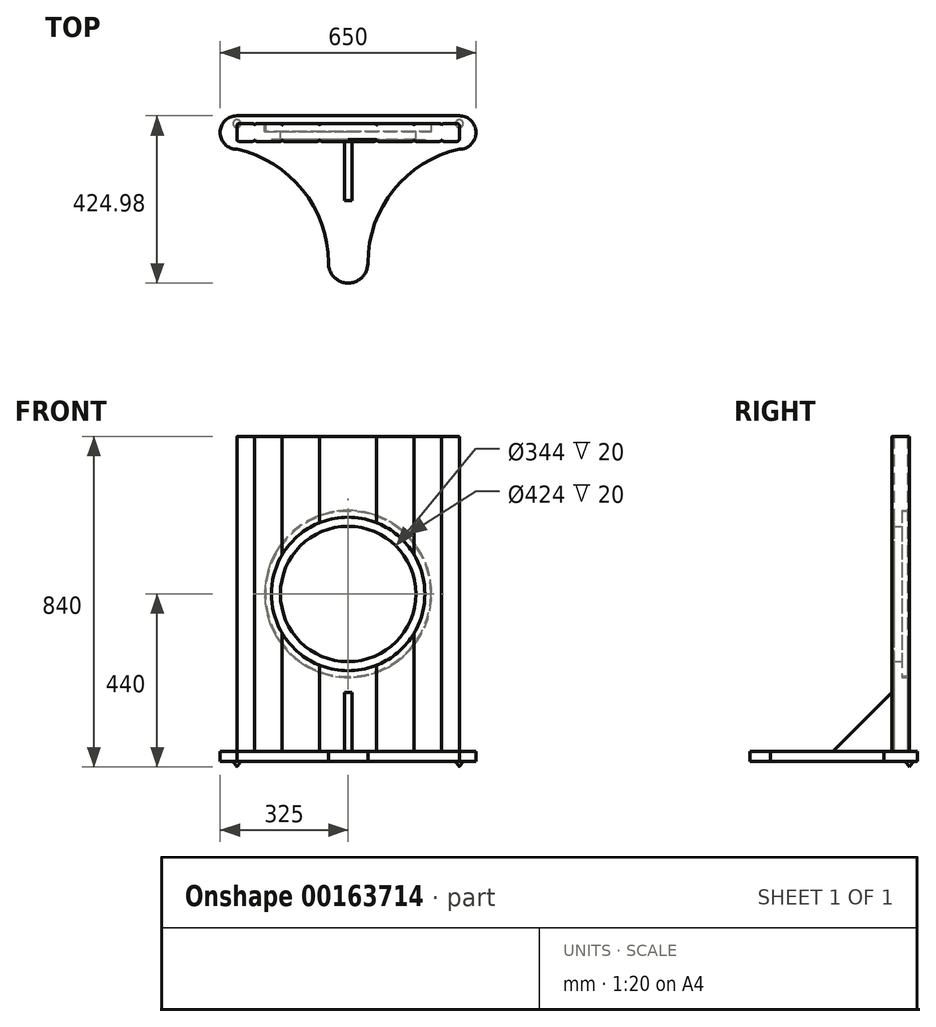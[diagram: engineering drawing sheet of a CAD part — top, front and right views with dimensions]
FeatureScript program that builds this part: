
annotation { "Feature Type Name" : "Feature", "Feature Type Description" : "" }
export const myFeature = defineFeature(function(context is Context, id is Id, definition is map)
    precondition{}
    {
        {
            var Q0;
            Q0=qCreatedBy(makeId("Top.planeOp"),FACE);
            var sketch = newSketch(context, id + "F0", { "sketchPlane" : qUnion([Q0])});
            skLineSegment(sketch, "E0.bottom", {"start": v(67.5, -22.5) * mm, "end": v(-67.5, -22.5) * mm});
            skLineSegment(sketch, "E0.top", {"start": v(67.5, 22.5) * mm, "end": v(-67.5, 22.5) * mm});
            skLineSegment(sketch, "E0.left", {"start": v(72.5, -17.5) * mm, "end": v(72.5, 17.5) * mm});
            skLineSegment(sketch, "E0.right", {"start": v(-72.5, -17.5) * mm, "end": v(-72.5, 17.5) * mm});
            skPoint(sketch, "E0.middle", {"position": v(0, 0) * mm});
            skPoint(sketch, "E1.visualSharp", {"position": v(-72.5, 22.5) * mm});
            skArc(sketch, "E1.filletArc", {"start": v(-67.5, 22.5) * mm, "mid": v(-71.04, 21.04) * mm, "end": v(-72.5, 17.5) * mm});
            skPoint(sketch, "E2.visualSharp", {"position": v(72.5, 22.5) * mm});
            skArc(sketch, "E2.filletArc", {"start": v(72.5, 17.5) * mm, "mid": v(71.04, 21.04) * mm, "end": v(67.5, 22.5) * mm});
            skPoint(sketch, "E3.visualSharp", {"position": v(72.5, -22.5) * mm});
            skArc(sketch, "E3.filletArc", {"start": v(67.5, -22.5) * mm, "mid": v(71.04, -21.04) * mm, "end": v(72.5, -17.5) * mm});
            skPoint(sketch, "E4.visualSharp", {"position": v(-72.5, -22.5) * mm});
            skArc(sketch, "E4.filletArc", {"start": v(-72.5, -17.5) * mm, "mid": v(-71.04, -21.04) * mm, "end": v(-67.5, -22.5) * mm});
            skSolve(sketch);
        }
        {
            var Q0;
            Q0 = qSketchRegion(id + "F0", true);
            extrude(context, id + "F1", {"entities" : qUnion([Q0]), "depth" : 800 * mm});
        }
        {
            var Q0;
            Q0=makeQuery(id+"F1.opExtrude","SWEPT_FACE",FACE,{"disambiguationData":[OSD([sQuery(id+"F0.wireOp",EDGE,"E0.right")])]});
            var sketch = newSketch(context, id + "F2", { "sketchPlane" : qUnion([Q0])});
            skLineSegment(sketch, "E5", {"start": v(-17.5, 0) * mm, "end": v(382.5, 0) * mm});
            skLineSegment(sketch, "E6", {"start": v(382.5, 0) * mm, "end": v(382.5, 50) * mm});
            skLineSegment(sketch, "E7", {"start": v(-17.5, 0) * mm, "end": v(-17.5, 500) * mm});
            skLineSegment(sketch, "E8", {"start": v(-17.5, 500) * mm, "end": v(17.5, 500) * mm});
            skArc(sketch, "E9", {"start": v(17.5, 500) * mm, "mid": v(117.94, 208.44) * mm, "end": v(382.5, 50) * mm});
            skSolve(sketch);
        }
        {
            var Q0;
            Q0 = qSketchRegion(id + "F2", true);
            extrude(context, id + "F3", {"entities" : qUnion([Q0]), "depth" : 10 * mm});
        }
        {
            var Q0;
            Q0=qCreatedBy(makeId("Top.planeOp"),FACE);
            var sketch = newSketch(context, id + "F4", { "sketchPlane" : qUnion([Q0])});
            skLineSegment(sketch, "E10.bottom", {"start": v(42.5, -22.5) * mm, "end": v(-42.5, -22.5) * mm});
            skLineSegment(sketch, "E10.top", {"start": v(42.5, 22.5) * mm, "end": v(-42.5, 22.5) * mm});
            skLineSegment(sketch, "E10.left", {"start": v(47.5, -17.5) * mm, "end": v(47.5, 17.5) * mm});
            skLineSegment(sketch, "E10.right", {"start": v(-47.5, -17.5) * mm, "end": v(-47.5, 17.5) * mm});
            skPoint(sketch, "E10.middle", {"position": v(0, 0) * mm});
            skPoint(sketch, "E11.visualSharp", {"position": v(-47.5, 22.5) * mm});
            skArc(sketch, "E11.filletArc", {"start": v(-42.5, 22.5) * mm, "mid": v(-46.04, 21.04) * mm, "end": v(-47.5, 17.5) * mm});
            skPoint(sketch, "E12.visualSharp", {"position": v(47.5, 22.5) * mm});
            skArc(sketch, "E12.filletArc", {"start": v(47.5, 17.5) * mm, "mid": v(46.04, 21.04) * mm, "end": v(42.5, 22.5) * mm});
            skPoint(sketch, "E13.visualSharp", {"position": v(47.5, -22.5) * mm});
            skArc(sketch, "E13.filletArc", {"start": v(42.5, -22.5) * mm, "mid": v(46.04, -21.04) * mm, "end": v(47.5, -17.5) * mm});
            skPoint(sketch, "E14.visualSharp", {"position": v(-47.5, -22.5) * mm});
            skArc(sketch, "E14.filletArc", {"start": v(-47.5, -17.5) * mm, "mid": v(-46.04, -21.04) * mm, "end": v(-42.5, -22.5) * mm});
            skSolve(sketch);
        }
        {
            var Q0;
            Q0 = qSketchRegion(id + "F4", true);
            extrude(context, id + "F5", {"entities" : qUnion([Q0]), "depth" : 800 * mm});
        }
        {
            var Q0;
            Q0=qCreatedBy(makeId("Top.planeOp"),FACE);
            var sketch = newSketch(context, id + "F6", { "sketchPlane" : qUnion([Q0])});
            skLineSegment(sketch, "E15.bottom", {"start": v(17.5, -22.5) * mm, "end": v(-17.5, -22.5) * mm});
            skLineSegment(sketch, "E15.top", {"start": v(17.5, 22.5) * mm, "end": v(-17.5, 22.5) * mm});
            skLineSegment(sketch, "E15.left", {"start": v(22.5, -17.5) * mm, "end": v(22.5, 17.5) * mm});
            skLineSegment(sketch, "E15.right", {"start": v(-22.5, -17.5) * mm, "end": v(-22.5, 17.5) * mm});
            skPoint(sketch, "E15.middle", {"position": v(0, 0) * mm});
            skPoint(sketch, "E16.visualSharp", {"position": v(-22.5, 22.5) * mm});
            skArc(sketch, "E16.filletArc", {"start": v(-17.5, 22.5) * mm, "mid": v(-21.04, 21.04) * mm, "end": v(-22.5, 17.5) * mm});
            skPoint(sketch, "E17.visualSharp", {"position": v(22.5, 22.5) * mm});
            skArc(sketch, "E17.filletArc", {"start": v(22.5, 17.5) * mm, "mid": v(21.04, 21.04) * mm, "end": v(17.5, 22.5) * mm});
            skPoint(sketch, "E18.visualSharp", {"position": v(22.5, -22.5) * mm});
            skArc(sketch, "E18.filletArc", {"start": v(17.5, -22.5) * mm, "mid": v(21.04, -21.04) * mm, "end": v(22.5, -17.5) * mm});
            skPoint(sketch, "E19.visualSharp", {"position": v(-22.5, -22.5) * mm});
            skArc(sketch, "E19.filletArc", {"start": v(-22.5, -17.5) * mm, "mid": v(-21.04, -21.04) * mm, "end": v(-17.5, -22.5) * mm});
            skSolve(sketch);
        }
        {
            var Q0;
            Q0 = qSketchRegion(id + "F6", true);
            extrude(context, id + "F7", {"entities" : qUnion([Q0]), "depth" : 800 * mm});
        }
        {
            var Q0;
            Q0=makeQuery(id+"F5.opExtrude","SWEPT_BODY",BODY,{"disambiguationData":[OSD([sQuery(id+"F4.wireOp",EDGE,"E10.bottom"),sQuery(id+"F4.wireOp",EDGE,"E10.top"),sQuery(id+"F4.wireOp",EDGE,"E10.left"),sQuery(id+"F4.wireOp",EDGE,"E10.right"),sQuery(id+"F4.wireOp",EDGE,"E11.filletArc"),sQuery(id+"F4.wireOp",EDGE,"E12.filletArc"),sQuery(id+"F4.wireOp",EDGE,"E13.filletArc"),sQuery(id+"F4.wireOp",EDGE,"E14.filletArc")])]});
            var Q1;
            Q1=makeQuery(id+"F1.opExtrude","CAP_EDGE",EDGE,{"disambiguationData":[OSD([sQuery(id+"F0.wireOp",EDGE,"E0.bottom")])],"isStart":false});
            transform(context, id + "F8", {"entities" : qUnion([Q0]), "transformType" : TransformType.TRANSLATION_DISTANCE, "transformDirection" : qUnion([Q1]), "distance" : (145 / 2 + 95 / 2) * mm, "makeCopy" : false});
        }
        {
            var Q0;
            Q0=makeQuery(id+"F7.opExtrude","SWEPT_BODY",BODY,{"disambiguationData":[OSD([sQuery(id+"F6.wireOp",EDGE,"E15.bottom"),sQuery(id+"F6.wireOp",EDGE,"E15.top"),sQuery(id+"F6.wireOp",EDGE,"E15.left"),sQuery(id+"F6.wireOp",EDGE,"E15.right"),sQuery(id+"F6.wireOp",EDGE,"E16.filletArc"),sQuery(id+"F6.wireOp",EDGE,"E17.filletArc"),sQuery(id+"F6.wireOp",EDGE,"E18.filletArc"),sQuery(id+"F6.wireOp",EDGE,"E19.filletArc")])]});
            var Q1;
            Q1=makeQuery(id+"F5.opExtrude","CAP_EDGE",EDGE,{"disambiguationData":[OSD([sQuery(id+"F4.wireOp",EDGE,"E10.bottom")])],"isStart":false});
            transform(context, id + "F9", {"entities" : qUnion([Q0]), "transformType" : TransformType.TRANSLATION_DISTANCE, "transformDirection" : qUnion([Q1]), "distance" : (145 / 2 + 95 + 70 + 22.5) * mm, "makeCopy" : false});
        }
        {
            var Q0;
            Q0=qCreatedBy(makeId("Top.planeOp"),FACE);
            var sketch = newSketch(context, id + "F10", { "sketchPlane" : qUnion([Q0])});
            skLineSegment(sketch, "E20.bottom", {"start": v(30, -22.5) * mm, "end": v(-30, -22.5) * mm});
            skLineSegment(sketch, "E20.top", {"start": v(30, 22.5) * mm, "end": v(-30, 22.5) * mm});
            skLineSegment(sketch, "E20.left", {"start": v(35, -17.5) * mm, "end": v(35, 17.5) * mm});
            skLineSegment(sketch, "E20.right", {"start": v(-35, -17.5) * mm, "end": v(-35, 17.5) * mm});
            skPoint(sketch, "E20.middle", {"position": v(0, 0) * mm});
            skPoint(sketch, "E21.visualSharp", {"position": v(-35, 22.5) * mm});
            skArc(sketch, "E21.filletArc", {"start": v(-30, 22.5) * mm, "mid": v(-33.54, 21.04) * mm, "end": v(-35, 17.5) * mm});
            skPoint(sketch, "E22.visualSharp", {"position": v(35, 22.5) * mm});
            skArc(sketch, "E22.filletArc", {"start": v(35, 17.5) * mm, "mid": v(33.54, 21.04) * mm, "end": v(30, 22.5) * mm});
            skPoint(sketch, "E23.visualSharp", {"position": v(35, -22.5) * mm});
            skArc(sketch, "E23.filletArc", {"start": v(30, -22.5) * mm, "mid": v(33.54, -21.04) * mm, "end": v(35, -17.5) * mm});
            skPoint(sketch, "E24.visualSharp", {"position": v(-35, -22.5) * mm});
            skArc(sketch, "E24.filletArc", {"start": v(-35, -17.5) * mm, "mid": v(-33.54, -21.04) * mm, "end": v(-30, -22.5) * mm});
            skSolve(sketch);
        }
        {
            var Q0;
            Q0 = qSketchRegion(id + "F10", true);
            extrude(context, id + "F11", {"entities" : qUnion([Q0]), "depth" : 800 * mm});
        }
        {
            var Q0;
            Q0=makeQuery(id+"F11.opExtrude","SWEPT_BODY",BODY,{"disambiguationData":[OSD([sQuery(id+"F10.wireOp",EDGE,"E20.bottom"),sQuery(id+"F10.wireOp",EDGE,"E20.top"),sQuery(id+"F10.wireOp",EDGE,"E20.left"),sQuery(id+"F10.wireOp",EDGE,"E20.right"),sQuery(id+"F10.wireOp",EDGE,"E21.filletArc"),sQuery(id+"F10.wireOp",EDGE,"E22.filletArc"),sQuery(id+"F10.wireOp",EDGE,"E23.filletArc"),sQuery(id+"F10.wireOp",EDGE,"E24.filletArc")])]});
            var Q1;
            Q1=makeQuery(id+"F5.opExtrude","CAP_EDGE",EDGE,{"disambiguationData":[OSD([sQuery(id+"F4.wireOp",EDGE,"E10.bottom")])],"isStart":true});
            transform(context, id + "F12", {"entities" : qUnion([Q0]), "transformType" : TransformType.TRANSLATION_DISTANCE, "transformDirection" : qUnion([Q1]), "distance" : (145 / 2 + 95 + 35) * mm, "makeCopy" : false});
        }
        {
            var Q0;
            Q0=makeQuery(id+"F5.opExtrude","SWEPT_BODY",BODY,{"disambiguationData":[OSD([sQuery(id+"F4.wireOp",EDGE,"E10.bottom"),sQuery(id+"F4.wireOp",EDGE,"E10.top"),sQuery(id+"F4.wireOp",EDGE,"E10.left"),sQuery(id+"F4.wireOp",EDGE,"E10.right"),sQuery(id+"F4.wireOp",EDGE,"E11.filletArc"),sQuery(id+"F4.wireOp",EDGE,"E12.filletArc"),sQuery(id+"F4.wireOp",EDGE,"E13.filletArc"),sQuery(id+"F4.wireOp",EDGE,"E14.filletArc")])]});
            transform(context, id + "F13", {"entities" : qUnion([Q0]), "transformType" : TransformType.COPY});
        }
        {
            var Q0;
            Q0=makeQuery(id+"F13.opPattern","COPY",BODY,{"derivedFrom":makeQuery(id+"F5.opExtrude","SWEPT_BODY",BODY,{"disambiguationData":[OSD([sQuery(id+"F4.wireOp",EDGE,"E10.bottom"),sQuery(id+"F4.wireOp",EDGE,"E10.top"),sQuery(id+"F4.wireOp",EDGE,"E10.left"),sQuery(id+"F4.wireOp",EDGE,"E10.right"),sQuery(id+"F4.wireOp",EDGE,"E11.filletArc"),sQuery(id+"F4.wireOp",EDGE,"E12.filletArc"),sQuery(id+"F4.wireOp",EDGE,"E13.filletArc"),sQuery(id+"F4.wireOp",EDGE,"E14.filletArc")])]}),"instanceName":"1"});
            var Q1;
            Q1=makeQuery(id+"F1.opExtrude","CAP_EDGE",EDGE,{"disambiguationData":[OSD([sQuery(id+"F0.wireOp",EDGE,"E0.bottom")])],"isStart":true});
            transform(context, id + "F14", {"entities" : qUnion([Q0]), "transformType" : TransformType.TRANSLATION_DISTANCE, "transformDirection" : qUnion([Q1]), "distance" : (145 + 95) * mm, "oppositeDirection" : true, "makeCopy" : false});
        }
        {
            var Q0;
            Q0=makeQuery(id+"F11.opExtrude","SWEPT_BODY",BODY,{"disambiguationData":[OSD([sQuery(id+"F10.wireOp",EDGE,"E20.bottom"),sQuery(id+"F10.wireOp",EDGE,"E20.top"),sQuery(id+"F10.wireOp",EDGE,"E20.left"),sQuery(id+"F10.wireOp",EDGE,"E20.right"),sQuery(id+"F10.wireOp",EDGE,"E21.filletArc"),sQuery(id+"F10.wireOp",EDGE,"E22.filletArc"),sQuery(id+"F10.wireOp",EDGE,"E23.filletArc"),sQuery(id+"F10.wireOp",EDGE,"E24.filletArc")])]});
            transform(context, id + "F15", {"entities" : qUnion([Q0]), "transformType" : TransformType.COPY});
        }
        {
            var Q0;
            Q0=makeQuery(id+"F15.opPattern","COPY",BODY,{"derivedFrom":makeQuery(id+"F11.opExtrude","SWEPT_BODY",BODY,{"disambiguationData":[OSD([sQuery(id+"F10.wireOp",EDGE,"E20.bottom"),sQuery(id+"F10.wireOp",EDGE,"E20.top"),sQuery(id+"F10.wireOp",EDGE,"E20.left"),sQuery(id+"F10.wireOp",EDGE,"E20.right"),sQuery(id+"F10.wireOp",EDGE,"E21.filletArc"),sQuery(id+"F10.wireOp",EDGE,"E22.filletArc"),sQuery(id+"F10.wireOp",EDGE,"E23.filletArc"),sQuery(id+"F10.wireOp",EDGE,"E24.filletArc")])]}),"instanceName":"1"});
            var Q1;
            Q1=makeQuery(id+"F5.opExtrude","CAP_EDGE",EDGE,{"disambiguationData":[OSD([sQuery(id+"F4.wireOp",EDGE,"E10.bottom")])],"isStart":true});
            transform(context, id + "F16", {"entities" : qUnion([Q0]), "transformType" : TransformType.TRANSLATION_DISTANCE, "transformDirection" : qUnion([Q1]), "distance" : (145 + 95 + 95 + 70) * mm, "oppositeDirection" : true, "makeCopy" : false});
        }
        {
            var Q0;
            Q0=makeQuery(id+"F7.opExtrude","SWEPT_BODY",BODY,{"disambiguationData":[OSD([sQuery(id+"F6.wireOp",EDGE,"E15.bottom"),sQuery(id+"F6.wireOp",EDGE,"E15.top"),sQuery(id+"F6.wireOp",EDGE,"E15.left"),sQuery(id+"F6.wireOp",EDGE,"E15.right"),sQuery(id+"F6.wireOp",EDGE,"E16.filletArc"),sQuery(id+"F6.wireOp",EDGE,"E17.filletArc"),sQuery(id+"F6.wireOp",EDGE,"E18.filletArc"),sQuery(id+"F6.wireOp",EDGE,"E19.filletArc")])]});
            transform(context, id + "F17", {"entities" : qUnion([Q0]), "transformType" : TransformType.COPY});
        }
        {
            var Q0;
            Q0=makeQuery(id+"F17.opPattern","COPY",BODY,{"derivedFrom":makeQuery(id+"F7.opExtrude","SWEPT_BODY",BODY,{"disambiguationData":[OSD([sQuery(id+"F6.wireOp",EDGE,"E15.bottom"),sQuery(id+"F6.wireOp",EDGE,"E15.top"),sQuery(id+"F6.wireOp",EDGE,"E15.left"),sQuery(id+"F6.wireOp",EDGE,"E15.right"),sQuery(id+"F6.wireOp",EDGE,"E16.filletArc"),sQuery(id+"F6.wireOp",EDGE,"E17.filletArc"),sQuery(id+"F6.wireOp",EDGE,"E18.filletArc"),sQuery(id+"F6.wireOp",EDGE,"E19.filletArc")])]}),"instanceName":"1"});
            var Q1;
            Q1=makeQuery(id+"F5.opExtrude","CAP_EDGE",EDGE,{"disambiguationData":[OSD([sQuery(id+"F4.wireOp",EDGE,"E10.bottom")])],"isStart":true});
            transform(context, id + "F18", {"entities" : qUnion([Q0]), "transformType" : TransformType.TRANSLATION_DISTANCE, "transformDirection" : qUnion([Q1]), "distance" : (145 + 95 + 95 + 70 + 70 + 45) * mm, "oppositeDirection" : true, "makeCopy" : false});
        }
        {
            var Q0;
            Q0=makeQuery(id+"F7.opExtrude","SWEPT_BODY",BODY,{"disambiguationData":[OSD([sQuery(id+"F6.wireOp",EDGE,"E15.bottom"),sQuery(id+"F6.wireOp",EDGE,"E15.top"),sQuery(id+"F6.wireOp",EDGE,"E15.left"),sQuery(id+"F6.wireOp",EDGE,"E15.right"),sQuery(id+"F6.wireOp",EDGE,"E16.filletArc"),sQuery(id+"F6.wireOp",EDGE,"E17.filletArc"),sQuery(id+"F6.wireOp",EDGE,"E18.filletArc"),sQuery(id+"F6.wireOp",EDGE,"E19.filletArc")])]});
            var Q1;
            Q1=makeQuery(id+"F11.opExtrude","SWEPT_BODY",BODY,{"disambiguationData":[OSD([sQuery(id+"F10.wireOp",EDGE,"E20.bottom"),sQuery(id+"F10.wireOp",EDGE,"E20.top"),sQuery(id+"F10.wireOp",EDGE,"E20.left"),sQuery(id+"F10.wireOp",EDGE,"E20.right"),sQuery(id+"F10.wireOp",EDGE,"E21.filletArc"),sQuery(id+"F10.wireOp",EDGE,"E22.filletArc"),sQuery(id+"F10.wireOp",EDGE,"E23.filletArc"),sQuery(id+"F10.wireOp",EDGE,"E24.filletArc")])]});
            var Q2;
            Q2=makeQuery(id+"F5.opExtrude","SWEPT_BODY",BODY,{"disambiguationData":[OSD([sQuery(id+"F4.wireOp",EDGE,"E10.bottom"),sQuery(id+"F4.wireOp",EDGE,"E10.top"),sQuery(id+"F4.wireOp",EDGE,"E10.left"),sQuery(id+"F4.wireOp",EDGE,"E10.right"),sQuery(id+"F4.wireOp",EDGE,"E11.filletArc"),sQuery(id+"F4.wireOp",EDGE,"E12.filletArc"),sQuery(id+"F4.wireOp",EDGE,"E13.filletArc"),sQuery(id+"F4.wireOp",EDGE,"E14.filletArc")])]});
            var Q3;
            Q3=makeQuery(id+"F1.opExtrude","SWEPT_BODY",BODY,{"disambiguationData":[OSD([sQuery(id+"F0.wireOp",EDGE,"E0.bottom"),sQuery(id+"F0.wireOp",EDGE,"E0.top"),sQuery(id+"F0.wireOp",EDGE,"E0.left"),sQuery(id+"F0.wireOp",EDGE,"E0.right"),sQuery(id+"F0.wireOp",EDGE,"E1.filletArc"),sQuery(id+"F0.wireOp",EDGE,"E2.filletArc"),sQuery(id+"F0.wireOp",EDGE,"E3.filletArc"),sQuery(id+"F0.wireOp",EDGE,"E4.filletArc")])]});
            var Q4;
            Q4=makeQuery(id+"F13.opPattern","COPY",BODY,{"derivedFrom":makeQuery(id+"F5.opExtrude","SWEPT_BODY",BODY,{"disambiguationData":[OSD([sQuery(id+"F4.wireOp",EDGE,"E10.bottom"),sQuery(id+"F4.wireOp",EDGE,"E10.top"),sQuery(id+"F4.wireOp",EDGE,"E10.left"),sQuery(id+"F4.wireOp",EDGE,"E10.right"),sQuery(id+"F4.wireOp",EDGE,"E11.filletArc"),sQuery(id+"F4.wireOp",EDGE,"E12.filletArc"),sQuery(id+"F4.wireOp",EDGE,"E13.filletArc"),sQuery(id+"F4.wireOp",EDGE,"E14.filletArc")])]}),"instanceName":"1"});
            var Q5;
            Q5=makeQuery(id+"F15.opPattern","COPY",BODY,{"derivedFrom":makeQuery(id+"F11.opExtrude","SWEPT_BODY",BODY,{"disambiguationData":[OSD([sQuery(id+"F10.wireOp",EDGE,"E20.bottom"),sQuery(id+"F10.wireOp",EDGE,"E20.top"),sQuery(id+"F10.wireOp",EDGE,"E20.left"),sQuery(id+"F10.wireOp",EDGE,"E20.right"),sQuery(id+"F10.wireOp",EDGE,"E21.filletArc"),sQuery(id+"F10.wireOp",EDGE,"E22.filletArc"),sQuery(id+"F10.wireOp",EDGE,"E23.filletArc"),sQuery(id+"F10.wireOp",EDGE,"E24.filletArc")])]}),"instanceName":"1"});
            var Q6;
            Q6=makeQuery(id+"F17.opPattern","COPY",BODY,{"derivedFrom":makeQuery(id+"F7.opExtrude","SWEPT_BODY",BODY,{"disambiguationData":[OSD([sQuery(id+"F6.wireOp",EDGE,"E15.bottom"),sQuery(id+"F6.wireOp",EDGE,"E15.top"),sQuery(id+"F6.wireOp",EDGE,"E15.left"),sQuery(id+"F6.wireOp",EDGE,"E15.right"),sQuery(id+"F6.wireOp",EDGE,"E16.filletArc"),sQuery(id+"F6.wireOp",EDGE,"E17.filletArc"),sQuery(id+"F6.wireOp",EDGE,"E18.filletArc"),sQuery(id+"F6.wireOp",EDGE,"E19.filletArc")])]}),"instanceName":"1"});
            booleanBodies(context, id + "F19", {"operationType" : BooleanOperationType.UNION, "tools" : qUnion([Q0, Q1, Q2, Q3, Q4, Q5, Q6])});
        }
        {
            var Q0;
            Q0=makeQuery(id+"F3.opExtrude","SWEPT_BODY",BODY,{"disambiguationData":[OSD([sQuery(id+"F2.wireOp",EDGE,"E5"),sQuery(id+"F2.wireOp",EDGE,"E6"),sQuery(id+"F2.wireOp",EDGE,"E7"),sQuery(id+"F2.wireOp",EDGE,"E8"),sQuery(id+"F2.wireOp",EDGE,"E9")])]});
            var Q1;
            Q1=makeQuery(id+"F5.opExtrude","CAP_EDGE",EDGE,{"disambiguationData":[OSD([sQuery(id+"F4.wireOp",EDGE,"E10.bottom")])],"isStart":true});
            transform(context, id + "F20", {"entities" : qUnion([Q0]), "transformType" : TransformType.TRANSLATION_DISTANCE, "transformDirection" : qUnion([Q1]), "distance" : (95 + 70 + 45) * mm, "makeCopy" : true});
        }
        {
            var Q0;
            Q0=makeQuery(id+"F3.opExtrude","SWEPT_BODY",BODY,{"disambiguationData":[OSD([sQuery(id+"F2.wireOp",EDGE,"E5"),sQuery(id+"F2.wireOp",EDGE,"E6"),sQuery(id+"F2.wireOp",EDGE,"E7"),sQuery(id+"F2.wireOp",EDGE,"E8"),sQuery(id+"F2.wireOp",EDGE,"E9")])]});
            var Q1;
            Q1=makeQuery(id+"F13.opPattern","COPY",EDGE,{"derivedFrom":makeQuery(id+"F5.opExtrude","CAP_EDGE",EDGE,{"disambiguationData":[OSD([sQuery(id+"F4.wireOp",EDGE,"E10.bottom")])],"isStart":true}),"instanceName":"1"});
            transform(context, id + "F21", {"entities" : qUnion([Q0]), "transformType" : TransformType.TRANSLATION_DISTANCE, "transformDirection" : qUnion([Q1]), "distance" : (145 + 95 + 70 + 45 + 5) * mm, "oppositeDirection" : true, "makeCopy" : false});
        }
        {
            var Q0;
            Q0=makeQuery(id+"F1.opExtrude","SWEPT_FACE",FACE,{"disambiguationData":[OSD([sQuery(id+"F0.wireOp",EDGE,"E0.top")])]});
            var sketch = newSketch(context, id + "F22", { "sketchPlane" : qUnion([Q0])});
            skCircle(sketch, "E25", {"center": v(0, 400) * mm, "radius": 172 * mm});
            skPoint(sketch, "E25.centerSnap0", {"position": v(67.5, 400) * mm});
            skSolve(sketch);
        }
        {
            var Q0;
            Q0 = qSketchRegion(id + "F22", true);
            extrude(context, id + "F23", {"entities" : qUnion([Q0]), "operationType" : NewBodyOperationType.REMOVE, "endBound" : BoundingType.THROUGH_ALL, "oppositeDirection" : true, "depth" : 25 * mm});
        }
        {
            var Q0;
            {var subQ1=sQuery(id+"F0.wireOp",EDGE,"E2.filletArc");var subQ3=sQuery(id+"F0.wireOp",EDGE,"E1.filletArc");var subQ4=sQuery(id+"F0.wireOp",EDGE,"E0.top");Q0=makeQuery(id+"F23.boolean.opBoolean","SPLIT",FACE,{"disambiguationData":[TD([makeQuery(id+"F1.opExtrude","CAP_FACE",FACE,{"disambiguationData":[OSD([sQuery(id+"F0.wireOp",EDGE,"E0.bottom"),subQ4,sQuery(id+"F0.wireOp",EDGE,"E0.left"),sQuery(id+"F0.wireOp",EDGE,"E0.right"),subQ3,subQ1,sQuery(id+"F0.wireOp",EDGE,"E3.filletArc"),sQuery(id+"F0.wireOp",EDGE,"E4.filletArc")])],"isStart":false})])],"derivedFrom":makeQuery(id+"F1.opExtrude","SWEPT_FACE",FACE,{"disambiguationData":[OSD([subQ4])]})});}
            var sketch = newSketch(context, id + "F24", { "sketchPlane" : qUnion([Q0])});
            skCircle(sketch, "E26", {"center": v(0, 400) * mm, "radius": 212 * mm});
            skSolve(sketch);
        }
        {
            var Q0;
            Q0 = qSketchRegion(id + "F24", true);
            extrude(context, id + "F25", {"entities" : qUnion([Q0]), "operationType" : NewBodyOperationType.REMOVE, "oppositeDirection" : true, "depth" : 20 * mm});
        }
        {
            var Q0;
            {var subQ1=sQuery(id+"F0.wireOp",EDGE,"E4.filletArc");var subQ2=sQuery(id+"F0.wireOp",EDGE,"E3.filletArc");var subQ3=sQuery(id+"F0.wireOp",EDGE,"E0.bottom");Q0=makeQuery(id+"F23.boolean.opBoolean","SPLIT",FACE,{"disambiguationData":[TD([makeQuery(id+"F1.opExtrude","CAP_FACE",FACE,{"disambiguationData":[OSD([subQ3,sQuery(id+"F0.wireOp",EDGE,"E0.top"),sQuery(id+"F0.wireOp",EDGE,"E0.left"),sQuery(id+"F0.wireOp",EDGE,"E0.right"),sQuery(id+"F0.wireOp",EDGE,"E1.filletArc"),sQuery(id+"F0.wireOp",EDGE,"E2.filletArc"),subQ2,subQ1])],"isStart":false})])],"derivedFrom":makeQuery(id+"F1.opExtrude","SWEPT_FACE",FACE,{"disambiguationData":[OSD([subQ3])]})});}
            var sketch = newSketch(context, id + "F26", { "sketchPlane" : qUnion([Q0])});
            skCircle(sketch, "E27", {"center": v(0, 400) * mm, "radius": 195 * mm});
            skSolve(sketch);
        }
        {
            var Q0;
            Q0 = qSketchRegion(id + "F26", true);
            extrude(context, id + "F27", {"entities" : qUnion([Q0]), "operationType" : NewBodyOperationType.REMOVE, "oppositeDirection" : true, "depth" : 5 * mm});
        }
        {
            var Q0;
            Q0=makeQuery(id+"F25.boolean.opBoolean","COPY",FACE,{"derivedFrom":makeQuery(id+"F25.opExtrude","CAP_FACE",FACE,{"disambiguationData":[OSD([sQuery(id+"F24.wireOp",EDGE,"E26")])],"isStart":false})});
            var sketch = newSketch(context, id + "F28", { "sketchPlane" : qUnion([Q0])});
            skCircle(sketch, "E28", {"center": v(0, 400) * mm, "radius": 210 * mm});
            skSolve(sketch);
        }
        {
            var Q0;
            Q0 = qSketchRegion(id + "F28", true);
            extrude(context, id + "F29", {"entities" : qUnion([Q0]), "depth" : 20 * mm});
        }
        {
            var Q0;
            {var subQ0=makeQuery(id+"F7.opExtrude","CAP_FACE",FACE,{"disambiguationData":[OSD([sQuery(id+"F6.wireOp",EDGE,"E15.bottom"),sQuery(id+"F6.wireOp",EDGE,"E15.top"),sQuery(id+"F6.wireOp",EDGE,"E15.left"),sQuery(id+"F6.wireOp",EDGE,"E15.right"),sQuery(id+"F6.wireOp",EDGE,"E16.filletArc"),sQuery(id+"F6.wireOp",EDGE,"E17.filletArc"),sQuery(id+"F6.wireOp",EDGE,"E18.filletArc"),sQuery(id+"F6.wireOp",EDGE,"E19.filletArc")])],"isStart":true});var subQ1=makeQuery(id+"F11.opExtrude","CAP_FACE",FACE,{"disambiguationData":[OSD([sQuery(id+"F10.wireOp",EDGE,"E20.bottom"),sQuery(id+"F10.wireOp",EDGE,"E20.top"),sQuery(id+"F10.wireOp",EDGE,"E20.left"),sQuery(id+"F10.wireOp",EDGE,"E20.right"),sQuery(id+"F10.wireOp",EDGE,"E21.filletArc"),sQuery(id+"F10.wireOp",EDGE,"E22.filletArc"),sQuery(id+"F10.wireOp",EDGE,"E23.filletArc"),sQuery(id+"F10.wireOp",EDGE,"E24.filletArc")])],"isStart":true});var subQ2=makeQuery(id+"F5.opExtrude","CAP_FACE",FACE,{"disambiguationData":[OSD([sQuery(id+"F4.wireOp",EDGE,"E10.bottom"),sQuery(id+"F4.wireOp",EDGE,"E10.top"),sQuery(id+"F4.wireOp",EDGE,"E10.left"),sQuery(id+"F4.wireOp",EDGE,"E10.right"),sQuery(id+"F4.wireOp",EDGE,"E11.filletArc"),sQuery(id+"F4.wireOp",EDGE,"E12.filletArc"),sQuery(id+"F4.wireOp",EDGE,"E13.filletArc"),sQuery(id+"F4.wireOp",EDGE,"E14.filletArc")])],"isStart":true});Q0=makeQuery(id+"F19.opBoolean","MERGE",FACE,{"derivedFrom":[makeQuery(id+"F1.opExtrude","CAP_FACE",FACE,{"disambiguationData":[OSD([sQuery(id+"F0.wireOp",EDGE,"E0.bottom"),sQuery(id+"F0.wireOp",EDGE,"E0.top"),sQuery(id+"F0.wireOp",EDGE,"E0.left"),sQuery(id+"F0.wireOp",EDGE,"E0.right"),sQuery(id+"F0.wireOp",EDGE,"E1.filletArc"),sQuery(id+"F0.wireOp",EDGE,"E2.filletArc"),sQuery(id+"F0.wireOp",EDGE,"E3.filletArc"),sQuery(id+"F0.wireOp",EDGE,"E4.filletArc")])],"isStart":true}),subQ2,subQ0,subQ1,makeQuery(id+"F13.opPattern","COPY",FACE,{"derivedFrom":subQ2,"instanceName":"1"}),makeQuery(id+"F15.opPattern","COPY",FACE,{"derivedFrom":subQ1,"instanceName":"1"}),makeQuery(id+"F17.opPattern","COPY",FACE,{"derivedFrom":subQ0,"instanceName":"1"})]});}
            var sketch = newSketch(context, id + "F30", { "sketchPlane" : qUnion([Q0])});
            skLineSegment(sketch, "E29", {"start": v(-282.5, -42.5) * mm, "end": v(282.5, -42.5) * mm});
            skArc(sketch, "E30", {"start": v(-282.5, -42.5) * mm, "mid": v(-325, 0) * mm, "end": v(-282.5, 42.5) * mm});
            skArc(sketch, "E31", {"start": v(282.5, -42.5) * mm, "mid": v(325, 0) * mm, "end": v(282.5, 42.5) * mm});
            skArc(sketch, "E32", {"start": v(-49.97, 330.82) * mm, "mid": v(0, 382.48) * mm, "end": v(49.97, 330.82) * mm});
            skArc(sketch, "E33", {"start": v(-282.5, 42.5) * mm, "mid": v(-115.8, 145.98) * mm, "end": v(-49.97, 330.82) * mm});
            skArc(sketch, "E34", {"start": v(49.97, 330.82) * mm, "mid": v(115.8, 145.98) * mm, "end": v(282.5, 42.5) * mm});
            skSolve(sketch);
        }
        {
            var Q0;
            Q0 = qSketchRegion(id + "F30", true);
            extrude(context, id + "F31", {"entities" : qUnion([Q0]), "depth" : 25 * mm});
        }
        {
            var Q0;
            Q0=makeQuery(id+"F17.opPattern","COPY",FACE,{"derivedFrom":makeQuery(id+"F7.opExtrude","SWEPT_FACE",FACE,{"disambiguationData":[OSD([sQuery(id+"F6.wireOp",EDGE,"E15.top")])]}),"instanceName":"1"});
            var sketch = newSketch(context, id + "F32", { "sketchPlane" : qUnion([Q0])});
            skLineSegment(sketch, "E35", {"start": v(-282.5, -25) * mm, "end": v(-292.5, -25) * mm});
            skLineSegment(sketch, "E36", {"start": v(-292.5, -25) * mm, "end": v(-282.5, -40) * mm});
            skLineSegment(sketch, "E37", {"start": v(-282.5, -40) * mm, "end": v(-282.5, -25) * mm});
            skSolve(sketch);
        }
        {
            var Q0;
            Q0 = qSketchRegion(id + "F32", true);
            var Q1;
            Q1=sQuery(id+"F32.wireOp",EDGE,"E37");
            revolve(context, id + "F33", {"entities" : qUnion([Q0]), "axis" : qUnion([Q1]), "revolveType" : RevolveType.FULL});
        }
        {
            var Q0;
            Q0=makeQuery(id+"F7.opExtrude","SWEPT_FACE",FACE,{"disambiguationData":[OSD([sQuery(id+"F6.wireOp",EDGE,"E15.top")])]});
            var sketch = newSketch(context, id + "F34", { "sketchPlane" : qUnion([Q0])});
            skLineSegment(sketch, "E38", {"start": v(282.5, -25) * mm, "end": v(292.5, -25) * mm});
            skLineSegment(sketch, "E39", {"start": v(292.5, -25) * mm, "end": v(282.5, -40) * mm});
            skLineSegment(sketch, "E40", {"start": v(282.5, -40) * mm, "end": v(282.5, -25) * mm});
            skSolve(sketch);
        }
        {
            var Q0;
            Q0 = qSketchRegion(id + "F34", true);
            var Q1;
            Q1=sQuery(id+"F34.wireOp",EDGE,"E40");
            revolve(context, id + "F35", {"entities" : qUnion([Q0]), "axis" : qUnion([Q1]), "revolveType" : RevolveType.FULL});
        }
        {
            var Q0;
            Q0=makeQuery(id+"F3.opExtrude","SWEPT_BODY",BODY,{"disambiguationData":[OSD([sQuery(id+"F2.wireOp",EDGE,"E5"),sQuery(id+"F2.wireOp",EDGE,"E6"),sQuery(id+"F2.wireOp",EDGE,"E7"),sQuery(id+"F2.wireOp",EDGE,"E8"),sQuery(id+"F2.wireOp",EDGE,"E9")])]});
            deleteBodies(context, id + "F36", {"entities" : qUnion([Q0])});
        }
        {
            var Q0;
            Q0=makeQuery(id+"F20.opPattern","COPY",BODY,{"derivedFrom":makeQuery(id+"F3.opExtrude","SWEPT_BODY",BODY,{"disambiguationData":[OSD([sQuery(id+"F2.wireOp",EDGE,"E5"),sQuery(id+"F2.wireOp",EDGE,"E6"),sQuery(id+"F2.wireOp",EDGE,"E7"),sQuery(id+"F2.wireOp",EDGE,"E8"),sQuery(id+"F2.wireOp",EDGE,"E9")])]}),"instanceName":"1"});
            deleteBodies(context, id + "F37", {"entities" : qUnion([Q0])});
        }
        {
            var Q0;
            Q0=qCreatedBy(makeId("Right.planeOp"),FACE);
            var sketch = newSketch(context, id + "F38", { "sketchPlane" : qUnion([Q0])});
            skLineSegment(sketch, "E41", {"start": v(-172.5, 0) * mm, "end": v(-22.5, 0) * mm});
            skLineSegment(sketch, "E42", {"start": v(-22.5, 0) * mm, "end": v(-22.5, 150) * mm});
            skLineSegment(sketch, "E43", {"start": v(-22.5, 150) * mm, "end": v(-172.5, 0) * mm});
            skSolve(sketch);
        }
        {
            var Q0;
            Q0 = qSketchRegion(id + "F38", true);
            extrude(context, id + "F39", {"entities" : qUnion([Q0]), "operationType" : NewBodyOperationType.ADD, "depth" : 19 * mm, "symmetric" : true});
        }
    });
